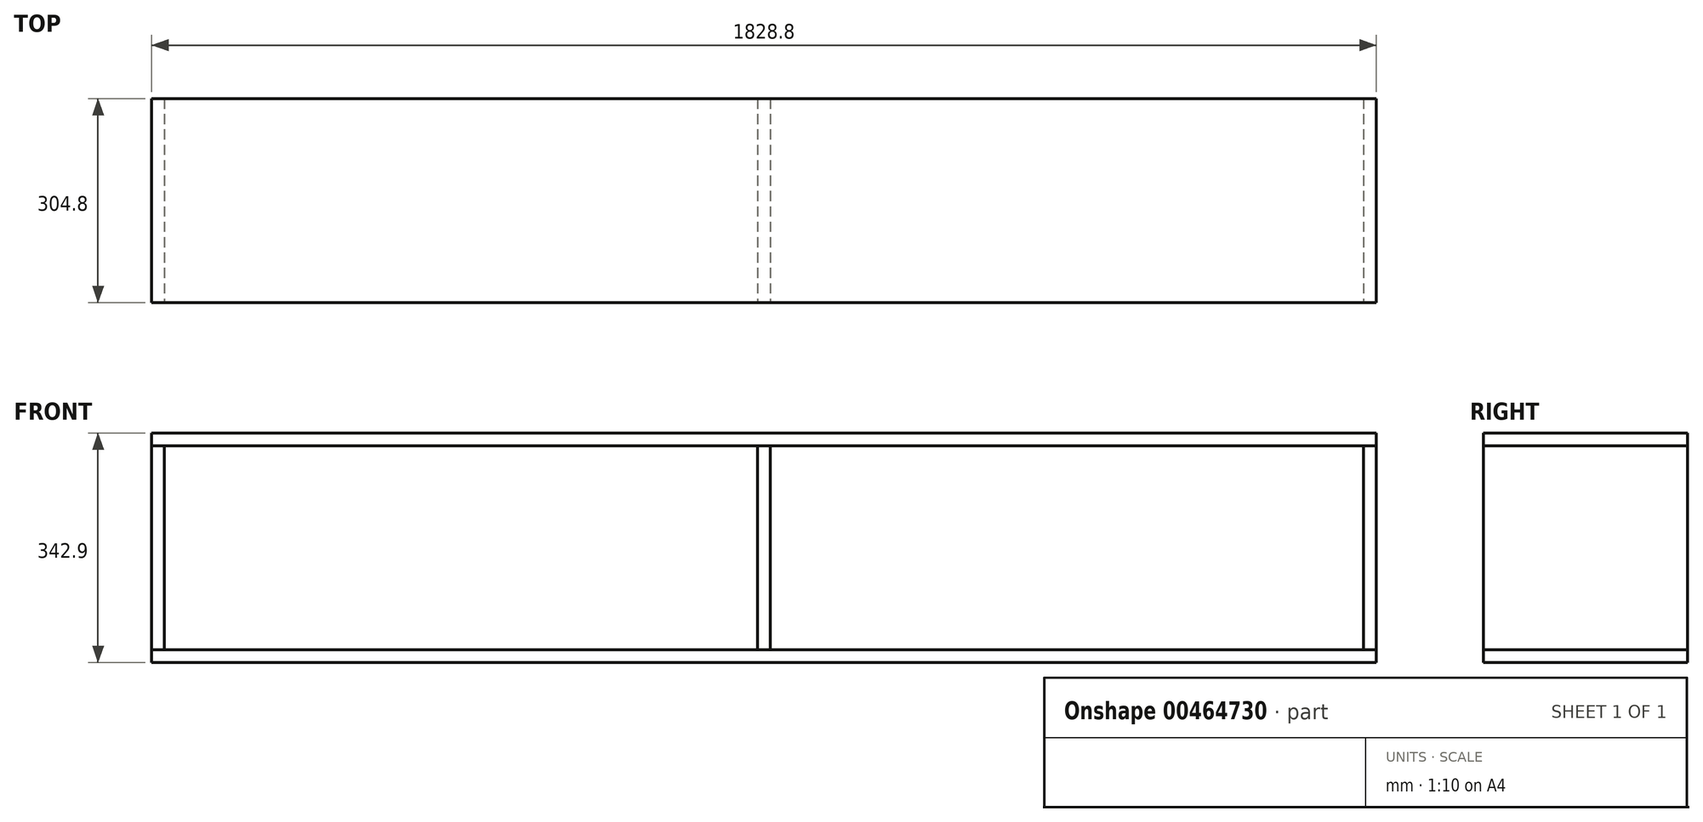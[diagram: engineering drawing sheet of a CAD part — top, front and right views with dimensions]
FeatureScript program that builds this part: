
annotation { "Feature Type Name" : "Feature", "Feature Type Description" : "" }
export const myFeature = defineFeature(function(context is Context, id is Id, definition is map)
    precondition{}
    {
        {
            var Q0;
            Q0=qCreatedBy(makeId("Front.planeOp"),FACE);
            var sketch = newSketch(context, id + "F0", { "sketchPlane" : qUnion([Q0])});
            skLineSegment(sketch, "E0.bottom", {"start": v(-911.87, -632.06) * mm, "end": v(916.93, -632.06) * mm});
            skLineSegment(sketch, "E0.top", {"start": v(-911.87, -327.26) * mm, "end": v(916.93, -327.26) * mm});
            skLineSegment(sketch, "E0.left", {"start": v(-911.87, -632.06) * mm, "end": v(-911.87, -327.26) * mm});
            skLineSegment(sketch, "E0.right", {"start": v(916.93, -632.06) * mm, "end": v(916.93, -327.26) * mm});
            skLineSegment(sketch, "E1", {"start": v(2.53, -327.26) * mm, "end": v(2.53, -632.06) * mm});
            skSolve(sketch);
        }
        {
            var Q0;
            Q0=sQuery(id+"F0.wireOp",EDGE,"E0.top");
            var Q1;
            Q1=sQuery(id+"F0.wireOp",EDGE,"E0.bottom");
            var Q2;
            Q2=sQuery(id+"F0.wireOp",EDGE,"E0.left");
            var Q3;
            Q3=sQuery(id+"F0.wireOp",EDGE,"E0.right");
            extrude(context, id + "F1", {"bodyType" : ToolBodyType.SURFACE, "surfaceEntities" : qUnion([Q0, Q1, Q2, Q3]), "depth" : 304.8 * mm});
        }
        {
            var Q0;
            Q0=sQuery(id+"F0.wireOp",EDGE,"E1");
            extrude(context, id + "F2", {"bodyType" : ToolBodyType.SURFACE, "surfaceEntities" : qUnion([Q0]), "depth" : 304.8 * mm});
        }
        {
            var Q0;
            Q0=makeQuery(id+"F1.opExtrude","SWEPT_FACE",FACE,{"disambiguationData":[OSD([sQuery(id+"F0.wireOp",EDGE,"E0.top")])]});
            extrude(context, id + "F3", {"entities" : qUnion([Q0]), "oppositeDirection" : true, "depth" : 19.05 * mm});
        }
        {
            var Q0;
            Q0=makeQuery(id+"F1.opExtrude","SWEPT_FACE",FACE,{"disambiguationData":[OSD([sQuery(id+"F0.wireOp",EDGE,"E0.bottom")])]});
            extrude(context, id + "F4", {"entities" : qUnion([Q0]), "oppositeDirection" : true, "depth" : 19.05 * mm});
        }
        {
            var Q0;
            Q0=makeQuery(id+"F1.opExtrude","SWEPT_FACE",FACE,{"disambiguationData":[OSD([sQuery(id+"F0.wireOp",EDGE,"E0.left")])]});
            extrude(context, id + "F5", {"entities" : qUnion([Q0]), "depth" : 19.05 * mm});
        }
        {
            var Q0;
            Q0=makeQuery(id+"F1.opExtrude","SWEPT_FACE",FACE,{"disambiguationData":[OSD([sQuery(id+"F0.wireOp",EDGE,"E0.right")])]});
            extrude(context, id + "F6", {"entities" : qUnion([Q0]), "depth" : 19.05 * mm});
        }
        {
            var Q0;
            Q0=makeQuery(id+"F2.opExtrude","SWEPT_FACE",FACE,{"disambiguationData":[OSD([sQuery(id+"F0.wireOp",EDGE,"E1")])]});
            extrude(context, id + "F7", {"entities" : qUnion([Q0]), "endBound" : BoundingType.SYMMETRIC, "depth" : 19.05 * mm});
        }
    });
